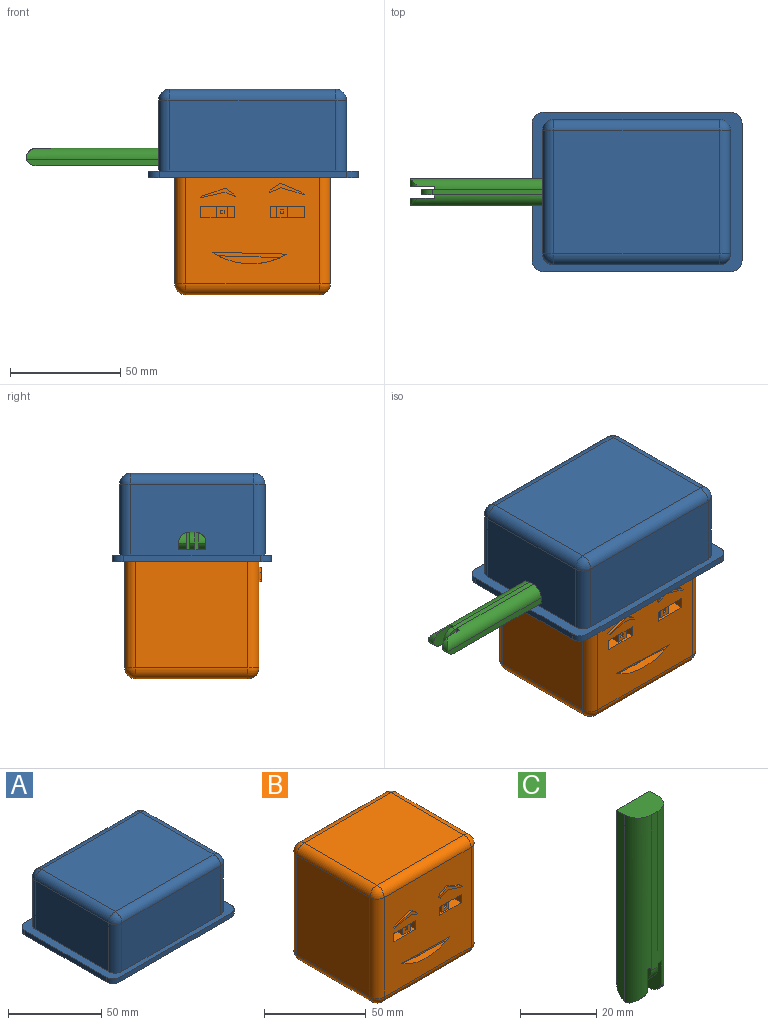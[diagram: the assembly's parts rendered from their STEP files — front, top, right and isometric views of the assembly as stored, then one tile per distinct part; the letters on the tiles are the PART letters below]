
ASSEMBLY  parts=3 mates=2
PART A: 32 faces, bbox 95x72x40 mm
  f0: plane 95x72mm, normal (0,0,-1), area 3778.5mm2, adj f2,f3,f4,f5,f6,f7,f8,f9
  f1: plane 95x72mm, normal (0,0,1), area 1240.8mm2, adj f2,f3,f4,f5,f6,f7,f8,f9
  f2: plane 85x3mm, normal (0,1,0), area 255mm2, adj f0,f1,f6,f9
  f3: plane 62x3mm, normal (-1,0,0), area 186mm2, adj f0,f1,f6,f7
  f4: plane 85x3mm, normal (0,-1,0), area 255mm2, adj f0,f1,f7,f8
  f5: plane 62x3mm, normal (1,0,0), area 186mm2, adj f0,f1,f8,f9
  f6: cylinder r=5mm len=5mm, axis (0,0,1), area 23.6mm2, adj f0,f1,f2,f3
  f7: cylinder r=5mm len=5mm, axis (0,0,-1), area 23.6mm2, adj f0,f1,f3,f4
  f8: cylinder r=5mm len=5mm, axis (0,0,1), area 23.6mm2, adj f0,f1,f4,f5
  f9: cylinder r=5mm len=5mm, axis (0,0,-1), area 23.6mm2, adj f0,f1,f2,f5
  f10: plane 75.08x32mm, normal (0,1,0), area 2402.7mm2, adj f1,f17,f23,f26
  f11: plane 55.81x32mm, normal (-1,0,0), area 1785.9mm2, adj f1,f20,f24,f26
  f12: plane 75.08x32mm, normal (0,-1,0), area 2402.7mm2, adj f1,f15,f19,f20
  f13: plane 55.81x32mm, normal (1,0,0), area 1785.9mm2, adj f1,f15,f17,f18
  f14: plane 75.08x55.81mm, normal (0,0,1), area 4190.3mm2, adj f18,f19,f23,f24
  f15: cylinder r=5mm len=32mm, axis (0,0,1), area 251.3mm2, adj f1,f12,f13,f16
  f16: sphere r=5mm, area 39.3mm2, adj f15,f18,f19
  f17: cylinder r=5mm len=32mm, axis (0,0,-1), area 251.3mm2, adj f1,f10,f13,f21
  f18: cylinder r=5mm len=55.81mm, axis (0,-1,0), area 438.3mm2, adj f13,f14,f16,f21
  f19: cylinder r=5mm len=75.08mm, axis (-1,0,0), area 589.7mm2, adj f12,f14,f16,f22
  f20: cylinder r=5mm len=32mm, axis (0,0,-1), area 251.3mm2, adj f1,f11,f12,f22
  f21: sphere r=5mm, area 39.3mm2, adj f17,f18,f23
  f22: sphere r=5mm, area 39.3mm2, adj f19,f20,f24
  f23: cylinder r=5mm len=75.08mm, axis (1,0,0), area 589.7mm2, adj f10,f14,f21,f25
  f24: cylinder r=5mm len=55.81mm, axis (0,1,0), area 438.3mm2, adj f11,f14,f22,f25
  f25: sphere r=5mm, area 39.3mm2, adj f23,f24,f26
  f26: cylinder r=5mm len=32mm, axis (0,0,1), area 251.3mm2, adj f1,f10,f11,f25
  f27: plane 60.8x17mm, normal (0,1,0), area 1033.6mm2, adj f0,f28,f30,f31
  f28: plane 50x17mm, normal (1,0,0), area 850mm2, adj f0,f27,f29,f31
  f29: plane 60.8x17mm, normal (0,-1,0), area 1033.6mm2, adj f0,f28,f30,f31
  f30: plane 50x17mm, normal (-1,0,0), area 850mm2, adj f0,f27,f29,f31
  f31: plane 60.8x50mm, normal (0,0,-1), area 3040mm2, adj f27,f28,f29,f30
PART B: 73 faces, bbox 70.5x61.8x70 mm
  f0: plane 60.5x60mm, normal (0,-1,0), area 3326.9mm2, adj f4,f6,f12,f16,f17,f18,f32,f33
  f1: plane 5x5mm, normal (0,-1,0), area 22mm2, adj f4,f36,f42,f43,f54,f55,f56,f57
  f2: plane 5x5mm, normal (0,-1,0), area 22.4mm2, adj f6,f32,f40,f41,f49,f50,f51,f52
  f3: plane 7.61x5mm, normal (0,-1,0), area 38.1mm2, adj f4,f36,f38,f43
  f4: plane 15.23x5mm, normal (0,0,1), area 56.1mm2, adj f0,f1,f3,f37,f38,f39,f42,f43
  f5: plane 5x3mm, normal (0,-1,0), area 15mm2, adj f6,f32,f34,f41
  f6: plane 15.23x5mm, normal (0,0,1), area 56.1mm2, adj f0,f2,f5,f33,f34,f35,f40,f41
  f7: plane 60.5x60mm, normal (0,1,0), area 3630.2mm2, adj f20,f25,f28,f31
  f8: plane 60x50.77mm, normal (-1,0,0), area 3046mm2, adj f17,f26,f27,f31
  f9: plane 60x50.77mm, normal (1,0,0), area 3046mm2, adj f12,f15,f19,f20
  f10: plane 60.5x50.77mm, normal (0,0,1), area 3071.6mm2, adj f15,f16,f25,f26
  f11: plane 60.5x50.77mm, normal (0,0,-1), area 3071.6mm2, adj f18,f19,f27,f28
  f12: cylinder r=5mm len=60mm, axis (0,0,1), area 471.2mm2, adj f0,f9,f13,f14
  f13: sphere r=5mm, area 39.3mm2, adj f12,f15,f16
  f14: sphere r=5mm, area 39.3mm2, adj f12,f18,f19
  f15: cylinder r=5mm len=50.77mm, axis (0,-1,0), area 398.7mm2, adj f9,f10,f13,f21
  f16: cylinder r=5mm len=60.5mm, axis (-1,0,0), area 475.2mm2, adj f0,f10,f13,f22
  f17: cylinder r=5mm len=60mm, axis (0,0,-1), area 471.2mm2, adj f0,f8,f22,f23
  f18: cylinder r=5mm len=60.5mm, axis (1,0,0), area 475.2mm2, adj f0,f11,f14,f23
  f19: cylinder r=5mm len=50.77mm, axis (0,1,0), area 398.7mm2, adj f9,f11,f14,f24
  f20: cylinder r=5mm len=60mm, axis (0,0,-1), area 471.2mm2, adj f7,f9,f21,f24
  f21: sphere r=5mm, area 39.3mm2, adj f15,f20,f25
  f22: sphere r=5mm, area 39.3mm2, adj f16,f17,f26
  f23: sphere r=5mm, area 39.3mm2, adj f17,f18,f27
  f24: sphere r=5mm, area 39.3mm2, adj f19,f20,f28
  f25: cylinder r=5mm len=60.5mm, axis (1,0,0), area 475.2mm2, adj f7,f10,f21,f29
  f26: cylinder r=5mm len=50.77mm, axis (0,1,0), area 398.7mm2, adj f8,f10,f22,f29
  f27: cylinder r=5mm len=50.77mm, axis (0,-1,0), area 398.7mm2, adj f8,f11,f23,f30
  f28: cylinder r=5mm len=60.5mm, axis (-1,0,0), area 475.2mm2, adj f7,f11,f24,f30
  f29: sphere r=5mm, area 39.3mm2, adj f25,f26,f31
  f30: sphere r=5mm, area 39.3mm2, adj f27,f28,f31
  f31: cylinder r=5mm len=60mm, axis (0,0,1), area 471.2mm2, adj f7,f8,f29,f30
  f32: plane 15.23x5mm, normal (0,0,-1), area 56.1mm2, adj f0,f2,f5,f33,f34,f35,f40,f41
  f33: plane 5x5mm, normal (1,0,0), area 25mm2, adj f0,f6,f32,f35
  f34: plane 5x5mm, normal (-1,0,0), area 25mm2, adj f0,f5,f6,f32
  f35: plane 7.23x5mm, normal (0,-1,0), area 36.1mm2, adj f6,f32,f33,f40
  f36: plane 15.23x5mm, normal (0,0,-1), area 56.1mm2, adj f0,f1,f3,f37,f38,f39,f42,f43
  f37: plane 5x5mm, normal (1,0,0), area 25mm2, adj f0,f4,f36,f39
  f38: plane 5x5mm, normal (-1,0,0), area 25mm2, adj f0,f3,f4,f36
  f39: plane 5x2.61mm, normal (0,-1,0), area 13.1mm2, adj f4,f36,f37,f42
  f40: plane 5x4mm, normal (-1,0,0), area 20mm2, adj f2,f6,f32,f35
  f41: plane 5x4mm, normal (1,0,0), area 20mm2, adj f2,f5,f6,f32
  f42: plane 5x4mm, normal (-1,0,0), area 20mm2, adj f1,f4,f36,f39
  f43: plane 5x4mm, normal (1,0,0), area 20mm2, adj f1,f3,f4,f36
  f44: cylinder r=31.83mm len=33.74mm, axis (0,-1,0), area 122.7mm2, adj f0,f45,f46,f47,f48
  f45: plane 33.74x1mm, normal (-0.02,0,-1), area 33.8mm2, adj f0,f44,f46
  f46: plane 33.74x2.4mm, normal (0,-1,0), area 49.3mm2, adj f44,f45,f47
  f47: plane 28.03x3mm, normal (-0.03,0,-1), area 84.1mm2, adj f44,f46,f48
  f48: plane 28.03x3.66mm, normal (0,-1,0), area 61.5mm2, adj f44,f47
  f49: plane 1.64x1mm, normal (0,0,-1), area 1.6mm2, adj f2,f50,f52,f53
  f50: plane 1.58x1mm, normal (1,0,0), area 1.6mm2, adj f2,f49,f51,f53
  f51: plane 1.64x1mm, normal (0,0,1), area 1.6mm2, adj f2,f50,f52,f53
  f52: plane 1.58x1mm, normal (-1,0,0), area 1.6mm2, adj f2,f49,f51,f53
  f53: plane 1.64x1.58mm, normal (0,-1,0), area 2.6mm2, adj f49,f50,f51,f52
  f54: plane 1.71x1mm, normal (0,0,-1), area 1.7mm2, adj f1,f55,f57,f58
  f55: plane 1.73x1mm, normal (1,0,0), area 1.7mm2, adj f1,f54,f56,f58
  f56: plane 1.71x1mm, normal (0,0,1), area 1.7mm2, adj f1,f55,f57,f58
  f57: plane 1.73x1mm, normal (-1,0,0), area 1.7mm2, adj f1,f54,f56,f58
  f58: plane 1.73x1.71mm, normal (0,-1,0), area 3mm2, adj f54,f55,f56,f57
  f59: plane 1.11x1mm, normal (-0.61,0,0.79), area 1.4mm2, adj f0,f60,f64,f65
  f60: plane 11.26x2.53mm, normal (0.22,0,-0.98), area 11.5mm2, adj f0,f59,f61,f65
  f61: plane 4.8x2.03mm, normal (-0.39,0,-0.92), area 5.2mm2, adj f0,f60,f62,f65
  f62: plane 1.33x1mm, normal (0.87,0,0.5), area 1.5mm2, adj f0,f61,f63,f65
  f63: plane 3.89x2.53mm, normal (0.55,0,0.84), area 4.6mm2, adj f0,f62,f64,f65
  f64: plane 10.29x3.51mm, normal (-0.32,0,0.95), area 10.9mm2, adj f0,f59,f63,f65
  f65: plane 16.06x4.37mm, normal (0,-1,0), area 18.9mm2, adj f59,f60,f61,f62,f63,f64
  f66: plane 1.36x1mm, normal (-0.96,0,0.28), area 1.4mm2, adj f0,f67,f71,f72
  f67: plane 5.03x2.45mm, normal (0.44,0,-0.9), area 5.6mm2, adj f0,f66,f68,f72
  f68: plane 10.64x3.22mm, normal (-0.29,0,-0.96), area 11.1mm2, adj f0,f67,f69,f72
  f69: plane 1.1x1mm, normal (0.75,0,0.66), area 1.5mm2, adj f0,f68,f70,f72
  f70: plane 9.74x4.11mm, normal (0.39,0,0.92), area 10.6mm2, adj f0,f69,f71,f72
  f71: plane 4.56x3.08mm, normal (-0.56,0,0.83), area 5.5mm2, adj f0,f66,f70,f72
  f72: plane 15.67x5.21mm, normal (0,-1,0), area 21.4mm2, adj f66,f67,f68,f69,f70,f71
PART C: 19 faces, bbox 12.4x8x60 mm
  f0: plane 55.42x12.39mm, normal (0,1,0), area 655.5mm2, adj f3,f4,f5,f9,f10,f11,f12,f13
  f1: cylinder r=5mm len=60mm, axis (0,0,1), area 447.1mm2, adj f2,f3,f4,f6,f9,f11
  f2: cylinder r=5mm len=4.79mm, axis (-1,0,0), area 14.8mm2, adj f1,f11,f18
  f3: plane 12.39x8mm, normal (0,0,1), area 88.4mm2, adj f0,f1,f4,f5,f6,f7
  f4: plane 60x3mm, normal (-1,0,0), area 176.2mm2, adj f0,f1,f3,f18
  f5: plane 60x3mm, normal (1,0,0), area 176.2mm2, adj f0,f3,f7,f16
  f6: plane 50x2.39mm, normal (0,-1,0), area 119.6mm2, adj f1,f3,f7,f13,f14,f15
  f7: cylinder r=5mm len=60mm, axis (0,0,-1), area 446.3mm2, adj f3,f5,f6,f8,f10,f12
  f8: cylinder r=5mm len=4.76mm, axis (-1,0,0), area 14.1mm2, adj f7,f12,f16
  f9: plane 8x1.44mm, normal (0,0,-1), area 11.4mm2, adj f0,f1,f11,f14
  f10: plane 8x1.54mm, normal (0,0,-1), area 12.2mm2, adj f0,f7,f12,f13
  f11: plane 11.03x7.79mm, normal (1,0,0), area 77.6mm2, adj f0,f1,f2,f9,f18
  f12: plane 11.03x7.76mm, normal (-1,0,0), area 77.3mm2, adj f0,f7,f8,f10,f16
  f13: plane 8x6.03mm, normal (1,0,0), area 39mm2, adj f0,f6,f10,f15,f17
  f14: plane 8x6.03mm, normal (-1,0,0), area 39mm2, adj f0,f6,f9,f15,f17
  f15: cylinder r=5mm len=5mm, axis (1,0,0), area 18.8mm2, adj f6,f13,f14,f17
  f16: cylinder r=5mm len=4.58mm, axis (1,0,0), area 20.1mm2, adj f0,f5,f8,f12
  f17: cylinder r=5mm len=4.58mm, axis (1,0,0), area 13.9mm2, adj f0,f13,f14,f15
  f18: cylinder r=5mm len=4.58mm, axis (1,0,0), area 20.7mm2, adj f0,f2,f4,f11
PLACE A t=(-55.68,-5.37,40.34)mm
PLACE B t=(-45.95,-5.07,-12.66)mm
PLACE C rot(axis=(-0.58,0.58,-0.58),120deg) t=(-115.46,-10.64,45.69)mm
MATE fastened C.f3 <-> A.f11  axis (1,0,0) through (-88.26,-9.1,49.34)mm
MATE fastened A.f31 <-> B.f10  axis (0,0,-1) through (-45.69,-8.9,57.34)mm
